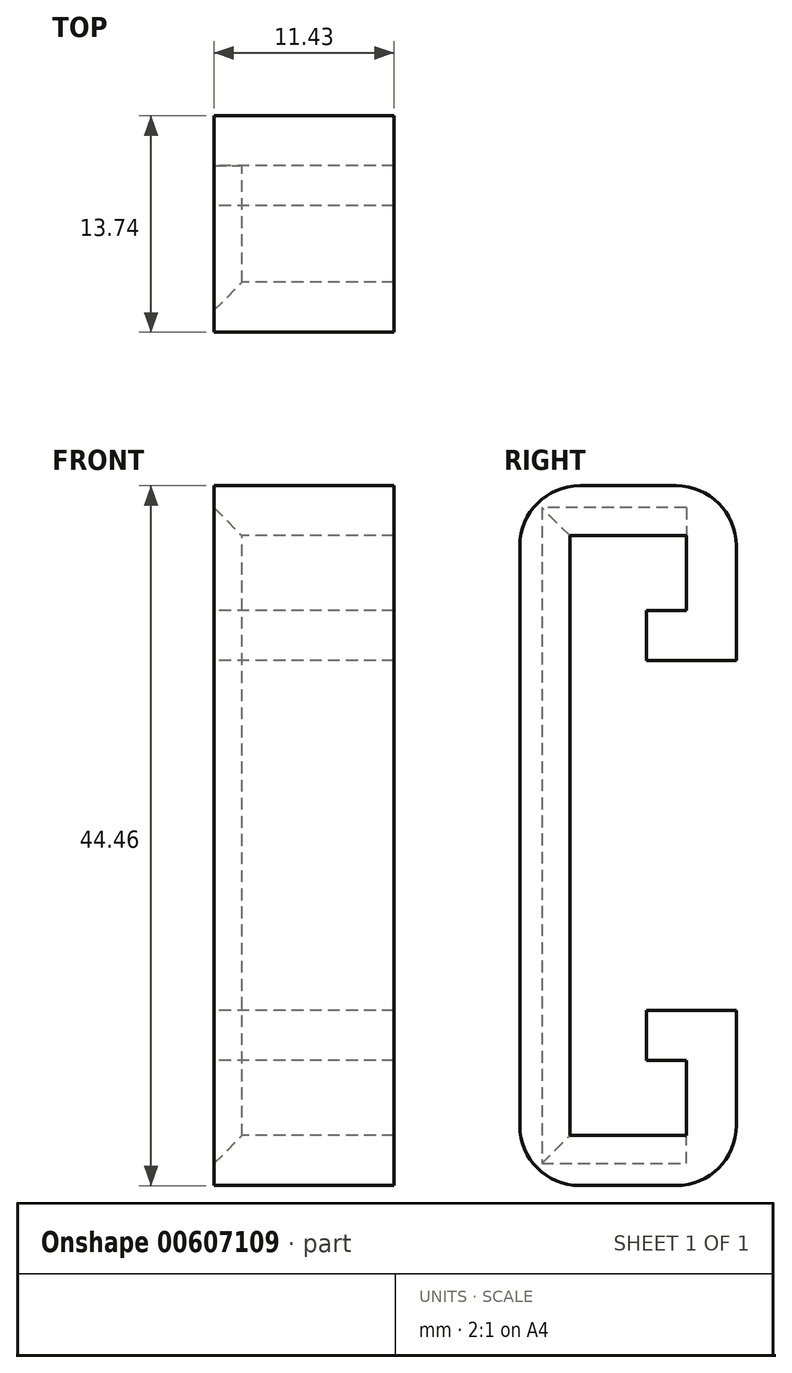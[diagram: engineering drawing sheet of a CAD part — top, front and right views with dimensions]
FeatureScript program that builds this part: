
annotation { "Feature Type Name" : "Feature", "Feature Type Description" : "" }
export const myFeature = defineFeature(function(context is Context, id is Id, definition is map)
    precondition{}
    {
        {
            var Q0;
            Q0=qCreatedBy(makeId("Right.planeOp"),FACE);
            var sketch = newSketch(context, id + "F0", { "sketchPlane" : qUnion([Q0])});
            skLineSegment(sketch, "E0", {"start": v(0, 0) * mm, "end": v(0, -19.05) * mm});
            skLineSegment(sketch, "E1", {"start": v(0, -19.05) * mm, "end": v(7.4, -19.05) * mm});
            skLineSegment(sketch, "E2", {"start": v(7.4, -19.05) * mm, "end": v(7.4, -14.29) * mm});
            skLineSegment(sketch, "E3", {"start": v(4.86, -11.11) * mm, "end": v(4.86, -14.29) * mm});
            skLineSegment(sketch, "E4.0", {"start": v(10.57, -18.41) * mm, "end": v(10.57, -11.11) * mm});
            skLineSegment(sketch, "E4.1", {"start": v(0.64, -22.23) * mm, "end": v(6.76, -22.23) * mm});
            skLineSegment(sketch, "E4.2", {"start": v(-3.18, 0) * mm, "end": v(-3.17, -18.41) * mm});
            skLineSegment(sketch, "E5", {"start": v(4.86, -14.29) * mm, "end": v(7.4, -14.29) * mm});
            skLineSegment(sketch, "E6", {"start": v(10.57, -11.11) * mm, "end": v(4.86, -11.11) * mm});
            skLineSegment(sketch, "E7", {"start": v(-3.18, 0) * mm, "end": v(0, 0) * mm, "construction": true});
            skLineSegment(sketch, "E8.MirrorCS", {"start": v(-3.18, 0) * mm, "end": v(-3.18, 18.41) * mm});
            skLineSegment(sketch, "E9.MirrorCS", {"start": v(0.63, 22.23) * mm, "end": v(6.76, 22.23) * mm});
            skLineSegment(sketch, "E10.MirrorCS", {"start": v(10.57, 18.42) * mm, "end": v(10.57, 11.11) * mm});
            skLineSegment(sketch, "E11.MirrorCS", {"start": v(10.57, 11.11) * mm, "end": v(4.86, 11.11) * mm});
            skLineSegment(sketch, "E12.MirrorCS", {"start": v(4.86, 11.11) * mm, "end": v(4.86, 14.29) * mm});
            skLineSegment(sketch, "E13.MirrorCS", {"start": v(4.86, 14.29) * mm, "end": v(7.4, 14.29) * mm});
            skLineSegment(sketch, "E14.MirrorCS", {"start": v(7.4, 19.05) * mm, "end": v(7.4, 14.29) * mm});
            skLineSegment(sketch, "E15.MirrorCS", {"start": v(0, 19.05) * mm, "end": v(7.4, 19.05) * mm});
            skLineSegment(sketch, "E16.MirrorCS", {"start": v(0, 0) * mm, "end": v(0, 19.05) * mm});
            skPoint(sketch, "E17.visualSharp", {"position": v(-3.17, -22.23) * mm});
            skArc(sketch, "E17.filletArc", {"start": v(-3.17, -18.41) * mm, "mid": v(-2.06, -21.1) * mm, "end": v(0.64, -22.23) * mm});
            skPoint(sketch, "E18.visualSharp", {"position": v(-3.18, 22.23) * mm});
            skArc(sketch, "E18.filletArc", {"start": v(0.63, 22.23) * mm, "mid": v(-2.06, 21.1) * mm, "end": v(-3.18, 18.41) * mm});
            skPoint(sketch, "E19.visualSharp", {"position": v(10.57, -22.23) * mm});
            skArc(sketch, "E19.filletArc", {"start": v(6.76, -22.23) * mm, "mid": v(9.46, -21.1) * mm, "end": v(10.57, -18.41) * mm});
            skPoint(sketch, "E20.visualSharp", {"position": v(10.57, 22.23) * mm});
            skArc(sketch, "E20.filletArc", {"start": v(10.57, 18.42) * mm, "mid": v(9.46, 21.1) * mm, "end": v(6.76, 22.23) * mm});
            skSolve(sketch);
        }
        {
            var Q0;
            Q0 = qSketchRegion(id + "F0", true);
            extrude(context, id + "F1", {"entities" : qUnion([Q0]), "endBound" : BoundingType.SYMMETRIC, "depth" : 11.43 * mm, "offsetDistance" : 25.4 * mm});
        }
        {
            var Q0;
            Q0=makeQuery(id+"F1.opExtrude","CAP_EDGE",EDGE,{"disambiguationData":[OSD([sQuery(id+"F0.wireOp",EDGE,"E1")])],"isStart":true});
            var Q1;
            Q1=makeQuery(id+"F1.opExtrude","CAP_EDGE",EDGE,{"disambiguationData":[OSD([sQuery(id+"F0.wireOp",EDGE,"E0"),sQuery(id+"F0.wireOp",EDGE,"E16.MirrorCS")])],"isStart":true});
            var Q2;
            Q2=makeQuery(id+"F1.opExtrude","CAP_EDGE",EDGE,{"disambiguationData":[OSD([sQuery(id+"F0.wireOp",EDGE,"E15.MirrorCS")])],"isStart":true});
            chamfer(context, id + "F2", {"entities" : qUnion([Q0, Q1, Q2]), "width" : 1.78 * mm, "tangentPropagation" : true});
        }
    });
